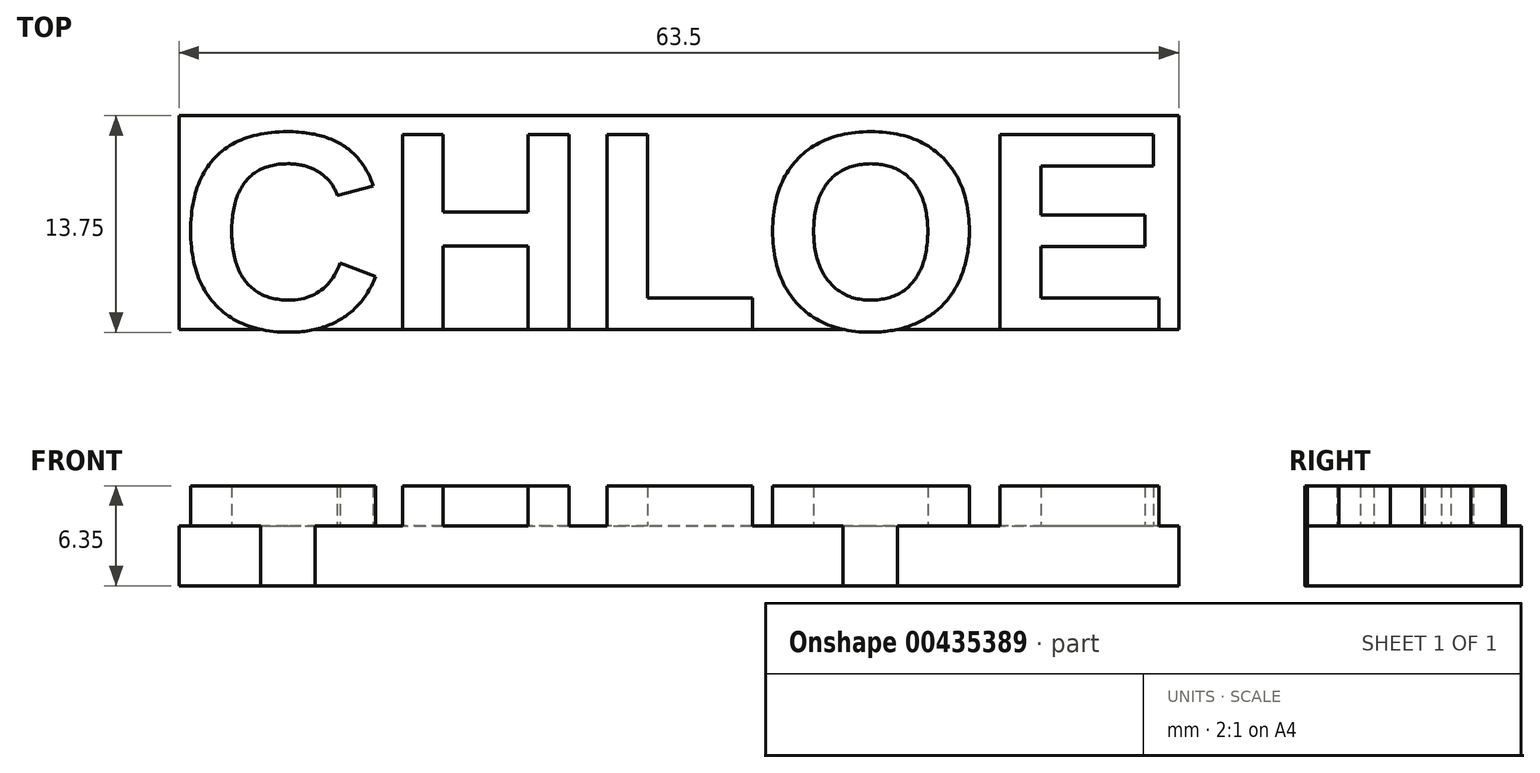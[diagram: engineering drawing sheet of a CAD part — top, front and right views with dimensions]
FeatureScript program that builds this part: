
annotation { "Feature Type Name" : "Feature", "Feature Type Description" : "" }
export const myFeature = defineFeature(function(context is Context, id is Id, definition is map)
    precondition{}
    {
        {
            var Q0;
            Q0=qCreatedBy(makeId("Top.planeOp"),FACE);
            var sketch = newSketch(context, id + "F0", { "sketchPlane" : qUnion([Q0])});
            skText(sketch, "E0", { "text": "CHLOE", "fontName": "Arimo-Bold.ttf"});
            const initialGuessF0  = {"E0": [0, 0, 1, 0, 0.01295]};
            skSetInitialGuess(sketch, initialGuessF0);
            skSolve(sketch);
        }
        {
            var Q0;
            Q0=qCreatedBy(makeId("Top.planeOp"),FACE);
            var sketch = newSketch(context, id + "F1", { "sketchPlane" : qUnion([Q0])});
            skLineSegment(sketch, "E1.bottom", {"start": v(0, 0) * mm, "end": v(63.5, 0) * mm});
            skLineSegment(sketch, "E1.top", {"start": v(0, 13.57) * mm, "end": v(63.5, 13.57) * mm});
            skLineSegment(sketch, "E1.left", {"start": v(0, 0) * mm, "end": v(0, 13.57) * mm});
            skLineSegment(sketch, "E1.right", {"start": v(63.5, 0) * mm, "end": v(63.5, 13.57) * mm});
            skSolve(sketch);
        }
        {
            var Q0;
            Q0=makeQuery(id+"F1.imprint","IMPRINT",FACE,{"disambiguationData":[TD([[makeQuery(id+"F1.imprint","IMPRINT",EDGE,{"derivedFrom":sQuery(id+"F1.wireOp",EDGE,"E1.bottom")}),1.0]])]});
            extrude(context, id + "F2", {"entities" : qUnion([Q0]), "depth" : 3.8 * mm});
        }
        {
            var Q0;
            Q0 = qSketchRegion(id + "F0", true);
            extrude(context, id + "F3", {"entities" : qUnion([Q0]), "operationType" : NewBodyOperationType.ADD, "depth" : 6.35 * mm});
        }
    });
